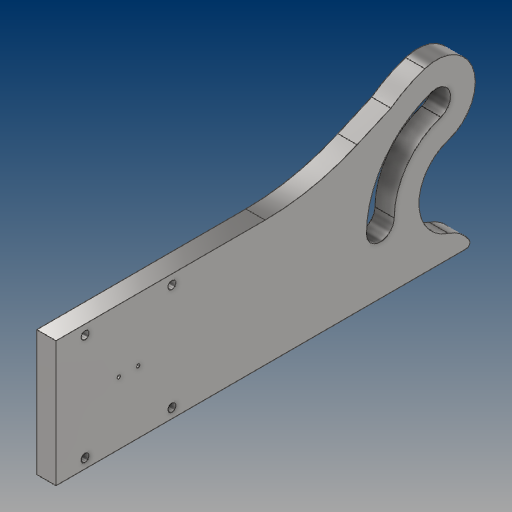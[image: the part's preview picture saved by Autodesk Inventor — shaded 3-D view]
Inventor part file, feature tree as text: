
AUTODESK INVENTOR PART (.ipt)
format: ipt  version: 2021 (Build 250183000, 183)  size: 194,560 bytes
history: native  units: mm
features: extrude x5, sketch x4, hole x2, fillet x2, chamfer x1, projected_geometry x1
ambient origin geometry x8: Origin, YZ Plane, XZ Plane, XY Plane, X Axis, Y Axis, Z Axis, Center Point
bodies: Solid1 (feature_tree)
feature tree (15):
  sketch  "Sketch1"  dims[d0=45.0mm d1=55.0mm]
  extrude  "Extrusion1"  Depth=55.0mm
  hole  "Hole1"  [1 undecoded]
  sketch  "Sketch3"  dims[d2=65.0mm d3=200.0mm]
  extrude  "Extrusion2"  Depth=10.0mm TaperAngle=0.0deg
  extrude  "Extrusion3"  Depth=2.0mm
  extrude  "Extrusion4"  Depth=20.0mm
  chamfer  "Chamfer1"  Distance=10.0mm
  fillet  "Fillet1"  Radius=80.0mm
  extrude  "Extrusion5"  Depth=7.2mm
  fillet  "Fillet2"  Radius=10.0mm
  hole  "Hole3"  [1 undecoded]
  projected_geometry  "Projected Loop2"
  sketch  "Sketch4"  dims[d4=15.0mm d5=10.0mm d6=0.0mm]
  sketch  "Sketch5"  dims[d7=4.2mm d8=6.0mm d9=4.0mm d10=2.0mm d11=90.0deg d12=8.0mm d13=20.594885mm d27=42.0mm d28=20.0mm d29=10.0mm d30=80.0mm d32=7.2mm d33=10.0mm d34=0.0mm d35=85.0mm d36=0.0mm d37=85.0mm d38=0.0mm d39=24.0mm d40=2.0mm d41=45.0deg d42=119.0mm d43=36.25mm d44=0.0mm d45=2.0mm d46=10.0mm d47=1.8mm d48=6.0mm d49=4.0mm d50=2.0mm d51=90.0deg d52=8.0mm d53=20.594885mm]
note: 2 required parameter values undecoded (feature->parameter linkage not recoverable at this tier; creation-order binding heuristic only, values carry confidence <= 0.55)
